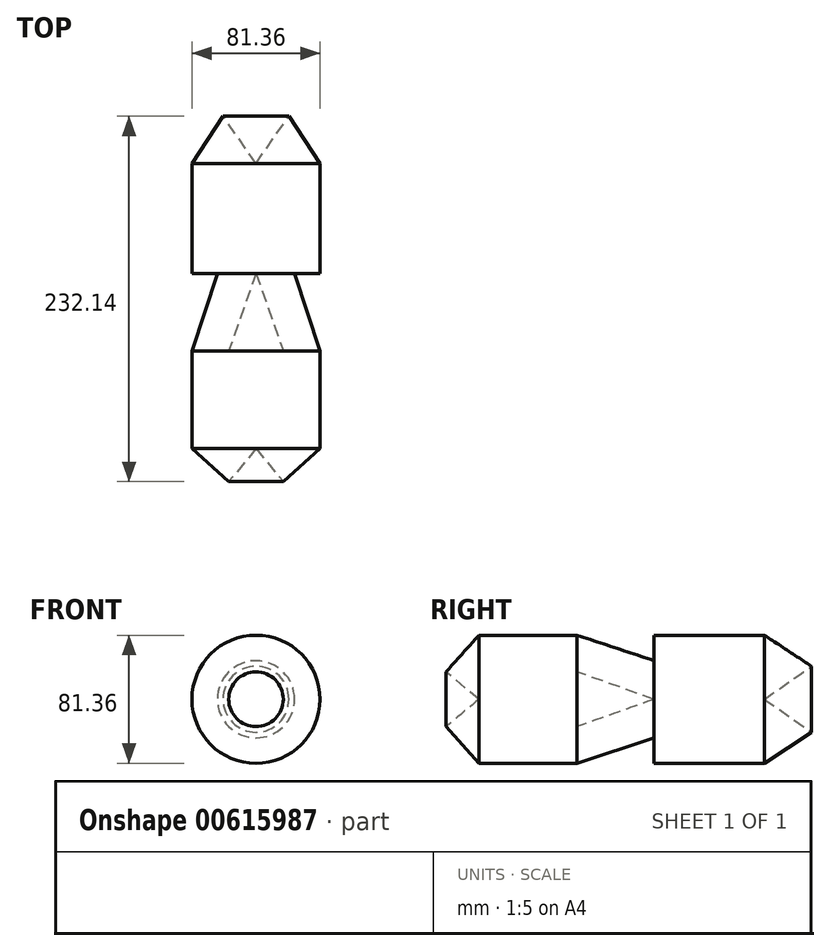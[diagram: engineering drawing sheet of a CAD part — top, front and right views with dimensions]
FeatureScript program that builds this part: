
annotation { "Feature Type Name" : "Feature", "Feature Type Description" : "" }
export const myFeature = defineFeature(function(context is Context, id is Id, definition is map)
    precondition{}
    {
        {
            var Q0;
            Q0=qCreatedBy(makeId("Top.planeOp"),FACE);
            var sketch = newSketch(context, id + "F0", { "sketchPlane" : qUnion([Q0])});
            skLineSegment(sketch, "E0", {"start": v(-35.88, 92.1) * mm, "end": v(-35.88, 22.1) * mm});
            skLineSegment(sketch, "E1", {"start": v(-14.94, 76.54) * mm, "end": v(-14.94, 32.86) * mm});
            skLineSegment(sketch, "E2", {"start": v(4.8, 92.1) * mm, "end": v(4.8, 22.1) * mm});
            skLineSegment(sketch, "E3", {"start": v(-35.88, -26.97) * mm, "end": v(-35.88, -89.19) * mm});
            skLineSegment(sketch, "E4", {"start": v(-14.94, -37.14) * mm, "end": v(-14.94, -82.6) * mm});
            skLineSegment(sketch, "E5", {"start": v(4.8, -89.19) * mm, "end": v(4.8, -26.97) * mm});
            skLineSegment(sketch, "E6", {"start": v(-35.88, 22.1) * mm, "end": v(-14.94, -37.14) * mm});
            skLineSegment(sketch, "E7", {"start": v(-14.94, 32.86) * mm, "end": v(4.8, -26.97) * mm});
            skLineSegment(sketch, "E8", {"start": v(-35.88, -26.97) * mm, "end": v(-18.54, -26.97) * mm});
            skLineSegment(sketch, "E9", {"start": v(4.8, 22.1) * mm, "end": v(-14.94, 22.1) * mm});
            skLineSegment(sketch, "E10", {"start": v(-35.88, 92.1) * mm, "end": v(-14.94, 122) * mm});
            skLineSegment(sketch, "E11", {"start": v(-14.94, 122) * mm, "end": v(4.8, 92.1) * mm});
            skLineSegment(sketch, "E12", {"start": v(-35.88, -89.19) * mm, "end": v(-18.54, -110.13) * mm});
            skLineSegment(sketch, "E13", {"start": v(-18.54, -110.13) * mm, "end": v(4.8, -89.19) * mm});
            skSolve(sketch);
        }
        {
            var Q0;
            {var subQ7=sQuery(id+"F0.wireOp",EDGE,"E0");Q0=makeQuery(id+"F0.imprint","IMPRINT",FACE,{"disambiguationData":[TD([[makeQuery(id+"F0.imprint","IMPRINT",EDGE,{"derivedFrom":subQ7}),1.0]])]});}
            var Q1;
            Q1=sQuery(id+"F0.wireOp",EDGE,"E0");
            revolve(context, id + "F1", {"entities" : qUnion([Q0]), "axis" : qUnion([Q1]), "revolveType" : RevolveType.FULL});
        }
    });
